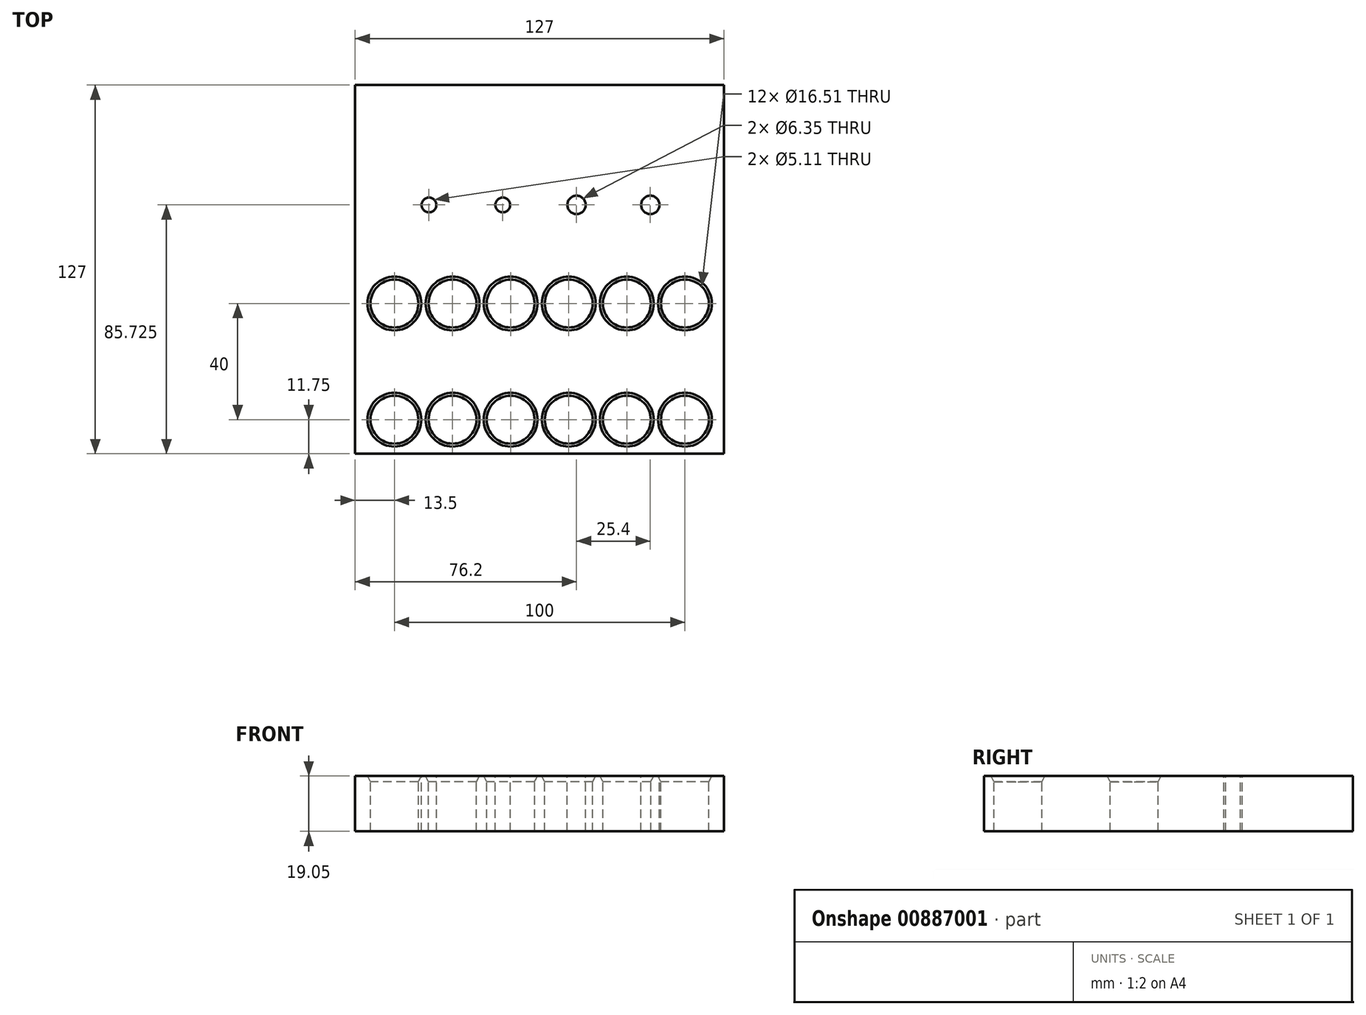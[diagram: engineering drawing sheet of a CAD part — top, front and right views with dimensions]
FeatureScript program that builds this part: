
annotation { "Feature Type Name" : "Feature", "Feature Type Description" : "" }
export const myFeature = defineFeature(function(context is Context, id is Id, definition is map)
    precondition{}
    {
        {
            var Q0;
            Q0=qCreatedBy(makeId("Top.planeOp"),FACE);
            var sketch = newSketch(context, id + "F0", { "sketchPlane" : qUnion([Q0])});
            skCircle(sketch, "E0", {"center": v(50, -11.75) * mm, "radius": 3.17 * mm, "construction": true});
            skCircle(sketch, "E1", {"center": v(50, -11.75) * mm, "radius": 8.26 * mm});
            skCircle(sketch, "E2.0.1.0", {"center": v(50, -51.75) * mm, "radius": 3.17 * mm, "construction": true});
            skCircle(sketch, "E2.0.1.1", {"center": v(50, -51.75) * mm, "radius": 8.26 * mm});
            skCircle(sketch, "E2.1.0.0", {"center": v(30, -11.75) * mm, "radius": 3.17 * mm, "construction": true});
            skCircle(sketch, "E2.1.0.1", {"center": v(30, -11.75) * mm, "radius": 8.26 * mm});
            skCircle(sketch, "E2.1.1.0", {"center": v(30, -51.75) * mm, "radius": 3.17 * mm, "construction": true});
            skCircle(sketch, "E2.1.1.1", {"center": v(30, -51.75) * mm, "radius": 8.26 * mm});
            skCircle(sketch, "E2.2.0.0", {"center": v(10, -11.75) * mm, "radius": 3.17 * mm, "construction": true});
            skCircle(sketch, "E2.2.0.1", {"center": v(10, -11.75) * mm, "radius": 8.26 * mm});
            skCircle(sketch, "E2.2.1.0", {"center": v(10, -51.75) * mm, "radius": 3.17 * mm, "construction": true});
            skCircle(sketch, "E2.2.1.1", {"center": v(10, -51.75) * mm, "radius": 8.26 * mm});
            skCircle(sketch, "E2.3.0.0", {"center": v(-10, -11.75) * mm, "radius": 3.17 * mm, "construction": true});
            skCircle(sketch, "E2.3.0.1", {"center": v(-10, -11.75) * mm, "radius": 8.26 * mm});
            skCircle(sketch, "E2.3.1.0", {"center": v(-10, -51.75) * mm, "radius": 3.17 * mm, "construction": true});
            skCircle(sketch, "E2.3.1.1", {"center": v(-10, -51.75) * mm, "radius": 8.26 * mm});
            skCircle(sketch, "E2.4.0.0", {"center": v(-30, -11.75) * mm, "radius": 3.17 * mm, "construction": true});
            skCircle(sketch, "E2.4.0.1", {"center": v(-30, -11.75) * mm, "radius": 8.26 * mm});
            skCircle(sketch, "E2.4.1.0", {"center": v(-30, -51.75) * mm, "radius": 3.17 * mm, "construction": true});
            skCircle(sketch, "E2.4.1.1", {"center": v(-30, -51.75) * mm, "radius": 8.26 * mm});
            skCircle(sketch, "E2.5.0.0", {"center": v(-50, -11.75) * mm, "radius": 3.17 * mm, "construction": true});
            skCircle(sketch, "E2.5.0.1", {"center": v(-50, -11.75) * mm, "radius": 8.26 * mm});
            skCircle(sketch, "E2.5.1.0", {"center": v(-50, -51.75) * mm, "radius": 3.17 * mm, "construction": true});
            skCircle(sketch, "E2.5.1.1", {"center": v(-50, -51.75) * mm, "radius": 8.26 * mm});
            skLineSegment(sketch, "E2.direction1", {"start": v(50, -11.75) * mm, "end": v(30, -11.75) * mm, "construction": true});
            skLineSegment(sketch, "E2.direction2", {"start": v(50, -11.75) * mm, "end": v(50, -51.75) * mm, "construction": true});
            skLineSegment(sketch, "E3.bottom", {"start": v(-63.5, 63.5) * mm, "end": v(63.5, 63.5) * mm});
            skLineSegment(sketch, "E3.top", {"start": v(-63.5, -63.5) * mm, "end": v(63.5, -63.5) * mm});
            skLineSegment(sketch, "E3.left", {"start": v(-63.5, 63.5) * mm, "end": v(-63.5, -63.5) * mm});
            skLineSegment(sketch, "E3.right", {"start": v(63.5, 63.5) * mm, "end": v(63.5, -63.5) * mm});
            skPoint(sketch, "E3.middle", {"position": v(0, 0) * mm});
            skPoint(sketch, "E4", {"position": v(50, -31.75) * mm});
            skCircle(sketch, "E5", {"center": v(-38.1, 22.22) * mm, "radius": 3.18 * mm});
            skCircle(sketch, "E6.1.0.0", {"center": v(-12.7, 22.22) * mm, "radius": 3.18 * mm});
            skLineSegment(sketch, "E6.direction1", {"start": v(-38.1, 22.22) * mm, "end": v(-12.7, 22.22) * mm, "construction": true});
            skLineSegment(sketch, "E7", {"start": v(0, 22.22) * mm, "end": v(0, 0) * mm, "construction": true});
            skCircle(sketch, "E8.MirrorC", {"center": v(12.7, 22.22) * mm, "radius": 3.18 * mm});
            skCircle(sketch, "E9.MirrorC", {"center": v(38.1, 22.23) * mm, "radius": 3.18 * mm});
            skLineSegment(sketch, "E10.bottom", {"start": v(-63.5, 63.5) * mm, "end": v(63.5, 63.5) * mm, "construction": true});
            skLineSegment(sketch, "E10.top", {"start": v(-63.5, 12.7) * mm, "end": v(63.5, 12.7) * mm, "construction": true});
            skLineSegment(sketch, "E10.left", {"start": v(-63.5, 63.5) * mm, "end": v(-63.5, 12.7) * mm, "construction": true});
            skLineSegment(sketch, "E10.right", {"start": v(63.5, 63.5) * mm, "end": v(63.5, 12.7) * mm, "construction": true});
            skSolve(sketch);
        }
        {
            var Q0;
            Q0=makeQuery(id+"F0.imprint","IMPRINT",FACE,{"disambiguationData":[TD([[makeQuery(id+"F0.imprint","IMPRINT",EDGE,{"derivedFrom":sQuery(id+"F0.wireOp",EDGE,"E1")}),-1.0]])]});
            var Q1;
            Q1=makeQuery(id+"F0.imprint","IMPRINT",FACE,{"disambiguationData":[TD([[makeQuery(id+"F0.imprint","IMPRINT",EDGE,{"derivedFrom":sQuery(id+"F0.wireOp",EDGE,"E5")}),1.0]])]});
            var Q2;
            Q2=makeQuery(id+"F0.imprint","IMPRINT",FACE,{"disambiguationData":[TD([[makeQuery(id+"F0.imprint","IMPRINT",EDGE,{"derivedFrom":sQuery(id+"F0.wireOp",EDGE,"E6.1.0.0")}),1.0]])]});
            var Q3;
            Q3=makeQuery(id+"F0.imprint","IMPRINT",FACE,{"disambiguationData":[TD([[makeQuery(id+"F0.imprint","IMPRINT",EDGE,{"derivedFrom":sQuery(id+"F0.wireOp",EDGE,"E8.MirrorC")}),-1.0]])]});
            var Q4;
            Q4=makeQuery(id+"F0.imprint","IMPRINT",FACE,{"disambiguationData":[TD([[makeQuery(id+"F0.imprint","IMPRINT",EDGE,{"derivedFrom":sQuery(id+"F0.wireOp",EDGE,"E9.MirrorC")}),-1.0]])]});
            var Q5;
            Q5=makeQuery(id+"F0.imprint","IMPRINT",FACE,{"disambiguationData":[TD([[makeQuery(id+"F0.imprint","IMPRINT",EDGE,{"derivedFrom":sQuery(id+"F0.wireOp",EDGE,"E1")}),1.0]])]});
            var Q6;
            Q6=makeQuery(id+"F0.imprint","IMPRINT",FACE,{"disambiguationData":[TD([[makeQuery(id+"F0.imprint","IMPRINT",EDGE,{"derivedFrom":sQuery(id+"F0.wireOp",EDGE,"E2.1.0.1")}),1.0]])]});
            var Q7;
            Q7=makeQuery(id+"F0.imprint","IMPRINT",FACE,{"disambiguationData":[TD([[makeQuery(id+"F0.imprint","IMPRINT",EDGE,{"derivedFrom":sQuery(id+"F0.wireOp",EDGE,"E2.2.0.1")}),1.0]])]});
            var Q8;
            Q8=makeQuery(id+"F0.imprint","IMPRINT",FACE,{"disambiguationData":[TD([[makeQuery(id+"F0.imprint","IMPRINT",EDGE,{"derivedFrom":sQuery(id+"F0.wireOp",EDGE,"E2.3.0.1")}),1.0]])]});
            var Q9;
            Q9=makeQuery(id+"F0.imprint","IMPRINT",FACE,{"disambiguationData":[TD([[makeQuery(id+"F0.imprint","IMPRINT",EDGE,{"derivedFrom":sQuery(id+"F0.wireOp",EDGE,"E2.4.0.1")}),1.0]])]});
            var Q10;
            Q10=makeQuery(id+"F0.imprint","IMPRINT",FACE,{"disambiguationData":[TD([[makeQuery(id+"F0.imprint","IMPRINT",EDGE,{"derivedFrom":sQuery(id+"F0.wireOp",EDGE,"E2.5.0.1")}),1.0]])]});
            var Q11;
            Q11=makeQuery(id+"F0.imprint","IMPRINT",FACE,{"disambiguationData":[TD([[makeQuery(id+"F0.imprint","IMPRINT",EDGE,{"derivedFrom":sQuery(id+"F0.wireOp",EDGE,"E2.5.1.1")}),1.0]])]});
            var Q12;
            Q12=makeQuery(id+"F0.imprint","IMPRINT",FACE,{"disambiguationData":[TD([[makeQuery(id+"F0.imprint","IMPRINT",EDGE,{"derivedFrom":sQuery(id+"F0.wireOp",EDGE,"E2.4.1.1")}),1.0]])]});
            var Q13;
            Q13=makeQuery(id+"F0.imprint","IMPRINT",FACE,{"disambiguationData":[TD([[makeQuery(id+"F0.imprint","IMPRINT",EDGE,{"derivedFrom":sQuery(id+"F0.wireOp",EDGE,"E2.3.1.1")}),1.0]])]});
            var Q14;
            Q14=makeQuery(id+"F0.imprint","IMPRINT",FACE,{"disambiguationData":[TD([[makeQuery(id+"F0.imprint","IMPRINT",EDGE,{"derivedFrom":sQuery(id+"F0.wireOp",EDGE,"E2.2.1.1")}),1.0]])]});
            var Q15;
            Q15=makeQuery(id+"F0.imprint","IMPRINT",FACE,{"disambiguationData":[TD([[makeQuery(id+"F0.imprint","IMPRINT",EDGE,{"derivedFrom":sQuery(id+"F0.wireOp",EDGE,"E2.1.1.1")}),1.0]])]});
            var Q16;
            Q16=makeQuery(id+"F0.imprint","IMPRINT",FACE,{"disambiguationData":[TD([[makeQuery(id+"F0.imprint","IMPRINT",EDGE,{"derivedFrom":sQuery(id+"F0.wireOp",EDGE,"E2.0.1.1")}),1.0]])]});
            extrude(context, id + "F1", {"entities" : qUnion([Q0, Q1, Q2, Q3, Q4, Q5, Q6, Q7, Q8, Q9, Q10, Q11, Q12, Q13, Q14, Q15, Q16]), "oppositeDirection" : true, "depth" : 19.05 * mm, "offsetDistance" : 25.4 * mm});
        }
        {
            var Q0;
            Q0=sQuery(id+"F0.wireOp",VERTEX,"E6.direction1.start");
            var Q1;
            Q1=sQuery(id+"F0.wireOp",VERTEX,"E6.direction1.end");
            var Q2;
            Q2=sQuery(id+"F0.wireOp",VERTEX,"E8.MirrorC.center");
            var Q3;
            Q3=sQuery(id+"F0.wireOp",VERTEX,"E9.MirrorC.center");
            var Q4;
            Q4=makeQuery(id+"F1.opExtrude","SWEPT_BODY",BODY,{"disambiguationData":[OSD([sQuery(id+"F0.wireOp",EDGE,"E1"),sQuery(id+"F0.wireOp",EDGE,"E2.0.1.1"),sQuery(id+"F0.wireOp",EDGE,"E2.1.0.1"),sQuery(id+"F0.wireOp",EDGE,"E2.1.1.1"),sQuery(id+"F0.wireOp",EDGE,"E2.2.0.1"),sQuery(id+"F0.wireOp",EDGE,"E2.2.1.1"),sQuery(id+"F0.wireOp",EDGE,"E2.3.0.1"),sQuery(id+"F0.wireOp",EDGE,"E2.3.1.1"),sQuery(id+"F0.wireOp",EDGE,"E2.4.0.1"),sQuery(id+"F0.wireOp",EDGE,"E2.4.1.1"),sQuery(id+"F0.wireOp",EDGE,"E2.5.0.1"),sQuery(id+"F0.wireOp",EDGE,"E2.5.1.1"),sQuery(id+"F0.wireOp",EDGE,"E3.bottom"),sQuery(id+"F0.wireOp",EDGE,"E3.top"),sQuery(id+"F0.wireOp",EDGE,"E3.left"),sQuery(id+"F0.wireOp",EDGE,"E3.right")])]});
            hole(context, id + "F2", {"style" : HoleStyle.SIMPLE, "endStyle" : HoleEndStyle.THROUGH, "standardTappedOrClearance" : lookupTablePath({ "standard" : "ANSI", "engagement" : "75%", "pitch" : "20 tpi", "size" : "1/4", "type" : "Tapped" }), "standardBlindInLast" : lookupTablePath({ "standard" : "ANSI", "engagement" : "75%", "pitch" : "20 tpi", "size" : "1/4", "type" : "Tapped" }), "holeDiameter" : 5.1 * mm, "majorDiameter" : 6.35 * mm, "showTappedDepth" : true, "isTappedThrough" : true, "tappedDepth" : 12.7 * mm, "tapClearance" : 3, "locations" : qUnion([Q0, Q1, Q2, Q3]), "scope" : qUnion([Q4])});
        }
        {
            var Q0;
            Q0=sQuery(id+"F0.wireOp",VERTEX,"E2.5.0.0.center");
            var Q1;
            Q1=sQuery(id+"F0.wireOp",VERTEX,"E2.4.0.0.center");
            var Q2;
            Q2=sQuery(id+"F0.wireOp",VERTEX,"E2.3.0.0.center");
            var Q3;
            Q3=sQuery(id+"F0.wireOp",VERTEX,"E2.2.0.0.center");
            var Q4;
            Q4=sQuery(id+"F0.wireOp",VERTEX,"E2.direction1.end");
            var Q5;
            Q5=sQuery(id+"F0.wireOp",VERTEX,"E2.direction1.start");
            var Q6;
            Q6=sQuery(id+"F0.wireOp",VERTEX,"E2.direction2.end");
            var Q7;
            Q7=sQuery(id+"F0.wireOp",VERTEX,"E2.1.1.0.center");
            var Q8;
            Q8=sQuery(id+"F0.wireOp",VERTEX,"E2.2.1.0.center");
            var Q9;
            Q9=sQuery(id+"F0.wireOp",VERTEX,"E2.3.1.0.center");
            var Q10;
            Q10=sQuery(id+"F0.wireOp",VERTEX,"E2.4.1.0.center");
            var Q11;
            Q11=sQuery(id+"F0.wireOp",VERTEX,"E2.5.1.0.center");
            var Q12;
            Q12=makeQuery(id+"F1.opExtrude","SWEPT_BODY",BODY,{"disambiguationData":[OSD([sQuery(id+"F0.wireOp",EDGE,"E3.bottom"),sQuery(id+"F0.wireOp",EDGE,"E3.top"),sQuery(id+"F0.wireOp",EDGE,"E3.left"),sQuery(id+"F0.wireOp",EDGE,"E3.right")])]});
            hole(context, id + "F3", {"style" : HoleStyle.C_SINK, "endStyle" : HoleEndStyle.THROUGH, "holeDiameter" : 16.5 * mm, "cSinkDiameter" : 18.54 * mm, "cSinkAngle" : 55 * degree, "majorDiameter" : 6.35 * mm, "isTappedThrough" : true, "tappedDepth" : 12.7 * mm, "tapClearance" : 3, "locations" : qUnion([Q0, Q1, Q2, Q3, Q4, Q5, Q6, Q7, Q8, Q9, Q10, Q11]), "scope" : qUnion([Q12])});
        }
    });
